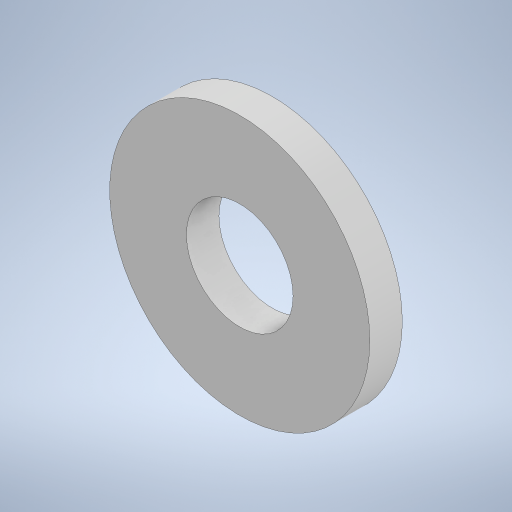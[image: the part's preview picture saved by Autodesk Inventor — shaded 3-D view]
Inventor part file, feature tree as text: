
AUTODESK INVENTOR PART (.ipt)
format: ipt  version: 2024.3 (Build 283343000, 343)  size: 223,744 bytes
history: native  units: mm
features: other x1, extrude x1, sketch x1
ambient origin geometry x8: Origin, YZ Plane, XZ Plane, XY Plane, X Axis, Y Axis, Z Axis, Center Point
bodies: Body1 (feature_tree)
feature tree (3):
  other  "ソリッド1"
  extrude  "押し出し1"  Depth=8.2mm
  sketch  "スケッチ1"
